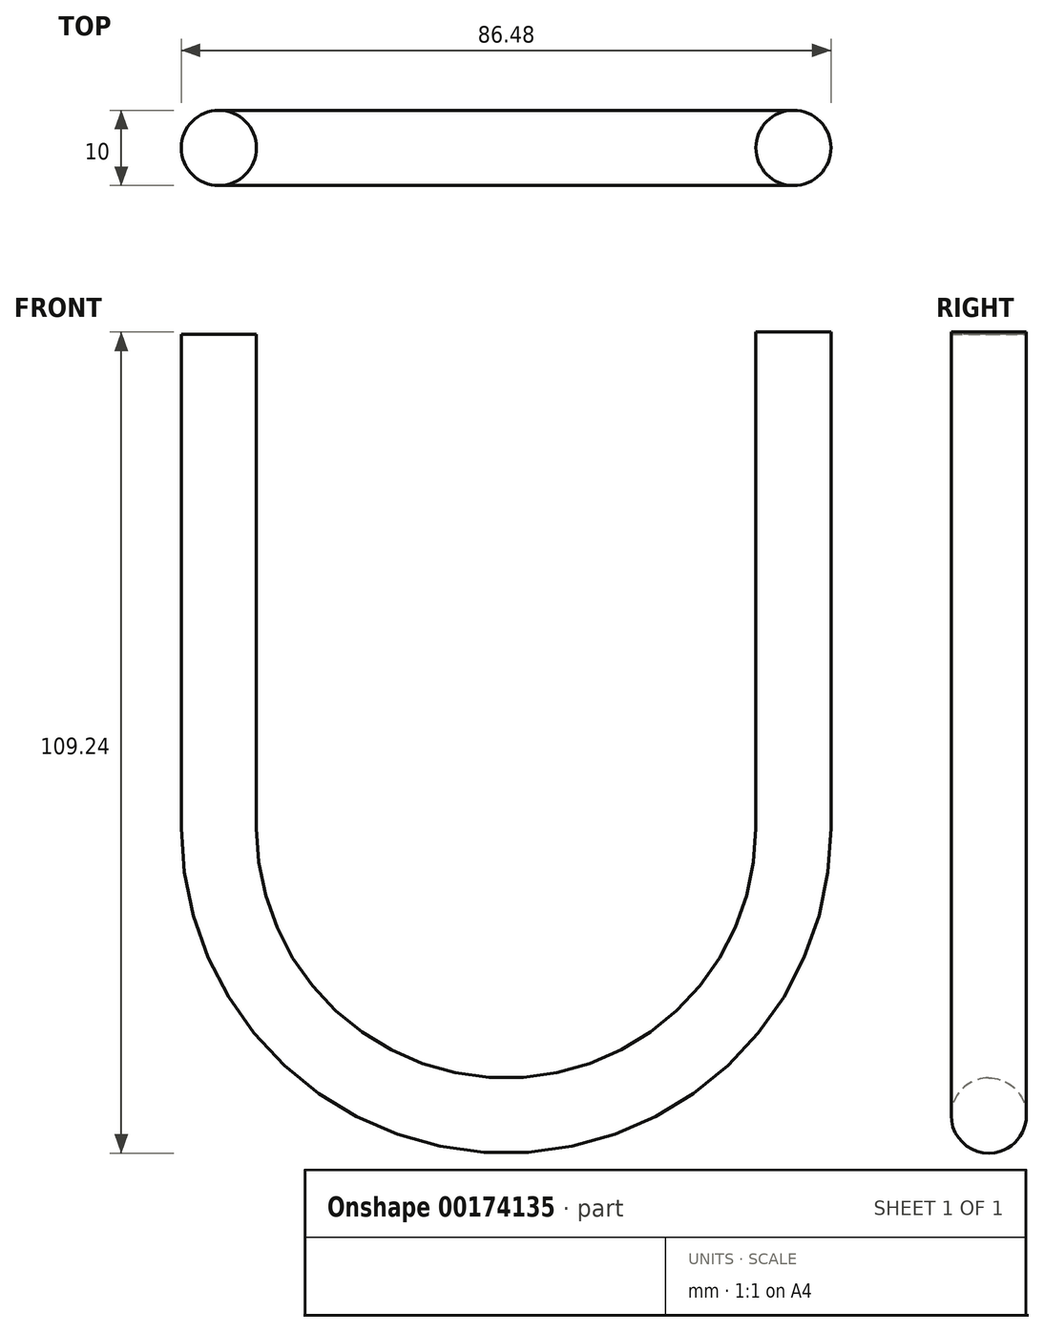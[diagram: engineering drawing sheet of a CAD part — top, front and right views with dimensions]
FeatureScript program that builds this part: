
annotation { "Feature Type Name" : "Feature", "Feature Type Description" : "" }
export const myFeature = defineFeature(function(context is Context, id is Id, definition is map)
    precondition{}
    {
        {
            var Q0;
            Q0=qCreatedBy(makeId("Front.planeOp"),FACE);
            var sketch = newSketch(context, id + "F0", { "sketchPlane" : qUnion([Q0])});
            skLineSegment(sketch, "E0", {"start": v(-38.95, 34.56) * mm, "end": v(-38.95, -31.16) * mm});
            skLineSegment(sketch, "E1", {"start": v(37.53, -31.16) * mm, "end": v(37.53, 34.84) * mm});
            skArc(sketch, "E2", {"start": v(-38.95, -31.16) * mm, "mid": v(-0.7, -69.4) * mm, "end": v(37.53, -31.16) * mm});
            skSolve(sketch);
        }
        {
            var Q0;
            Q0=qCreatedBy(makeId("Top.planeOp"),FACE);
            var sketch = newSketch(context, id + "F1", { "sketchPlane" : qUnion([Q0])});
            skCircle(sketch, "E3", {"center": v(-38.95, 0) * mm, "radius": 5 * mm});
            skSolve(sketch);
        }
        {
            var Q0;
            Q0=makeQuery(id+"F1.imprint","IMPRINT",FACE,{"disambiguationData":[TD([[makeQuery(id+"F1.imprint","IMPRINT",EDGE,{"derivedFrom":sQuery(id+"F1.wireOp",EDGE,"E3")}),1.0]])]});
            var Q1;
            Q1=sQuery(id+"F0.wireOp",EDGE,"E0");
            var Q2;
            Q2=sQuery(id+"F0.wireOp",EDGE,"E2");
            var Q3;
            Q3=sQuery(id+"F0.wireOp",EDGE,"E1");
            sweep(context, id + "F2", {"profiles" : qUnion([Q0]), "path" : qUnion([Q1, Q2, Q3])});
        }
    });
